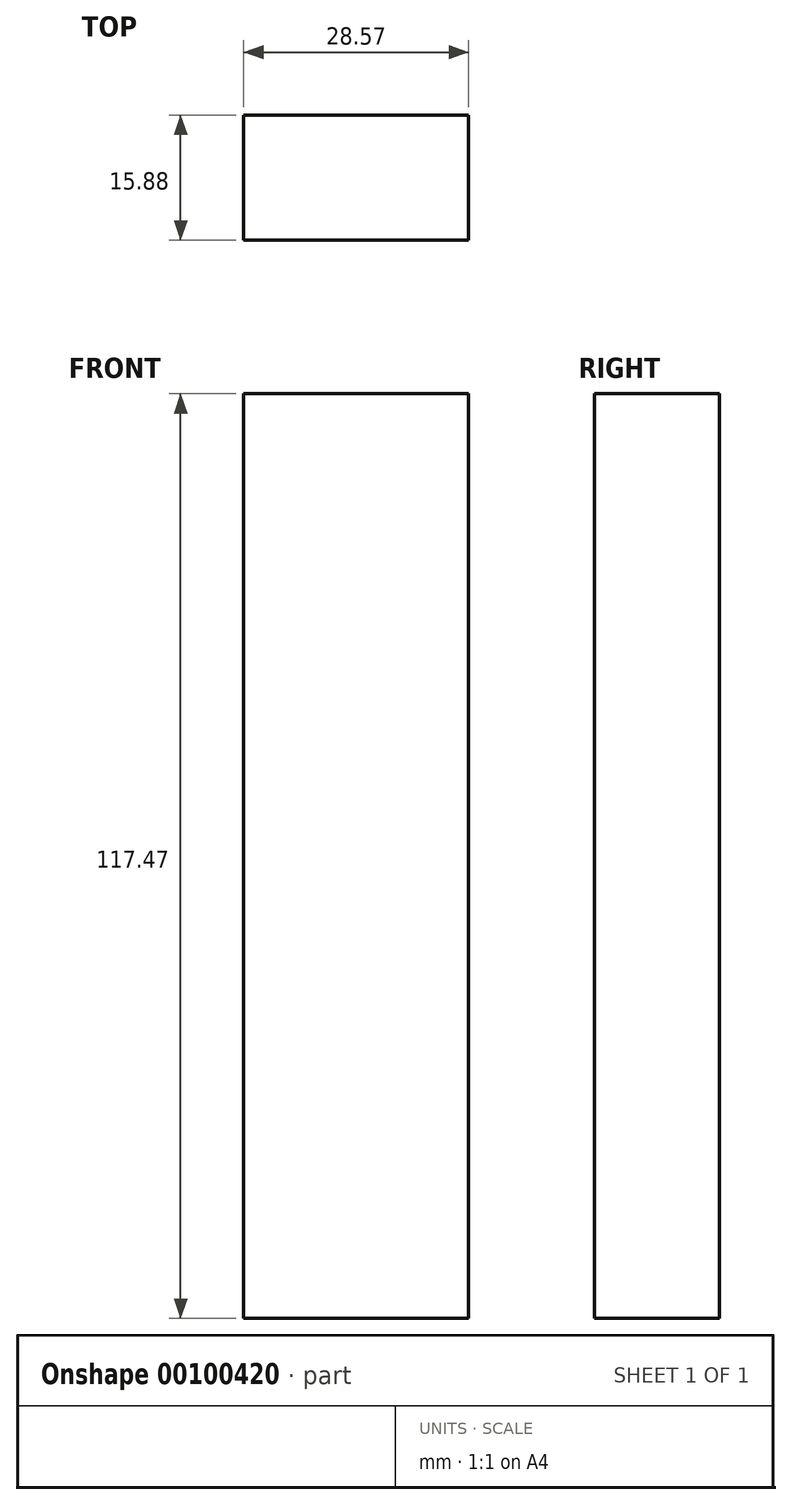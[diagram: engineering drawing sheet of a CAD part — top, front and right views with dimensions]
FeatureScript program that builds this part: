
annotation { "Feature Type Name" : "Feature", "Feature Type Description" : "" }
export const myFeature = defineFeature(function(context is Context, id is Id, definition is map)
    precondition{}
    {
        {
            var Q0;
            Q0=qCreatedBy(makeId("Top.planeOp"),FACE);
            var sketch = newSketch(context, id + "F0", { "sketchPlane" : qUnion([Q0])});
            skLineSegment(sketch, "E0.bottom", {"start": v(0, 0) * mm, "end": v(28.58, 0) * mm});
            skLineSegment(sketch, "E0.top", {"start": v(0, 15.88) * mm, "end": v(28.58, 15.88) * mm});
            skLineSegment(sketch, "E0.left", {"start": v(0, 0) * mm, "end": v(0, 15.88) * mm});
            skLineSegment(sketch, "E0.right", {"start": v(28.58, 0) * mm, "end": v(28.58, 15.87) * mm});
            skSolve(sketch);
        }
        {
            var Q0;
            Q0 = qSketchRegion(id + "F0", true);
            extrude(context, id + "F1", {"entities" : qUnion([Q0]), "oppositeDirection" : true, "depth" : 117.47 * mm});
        }
    });
